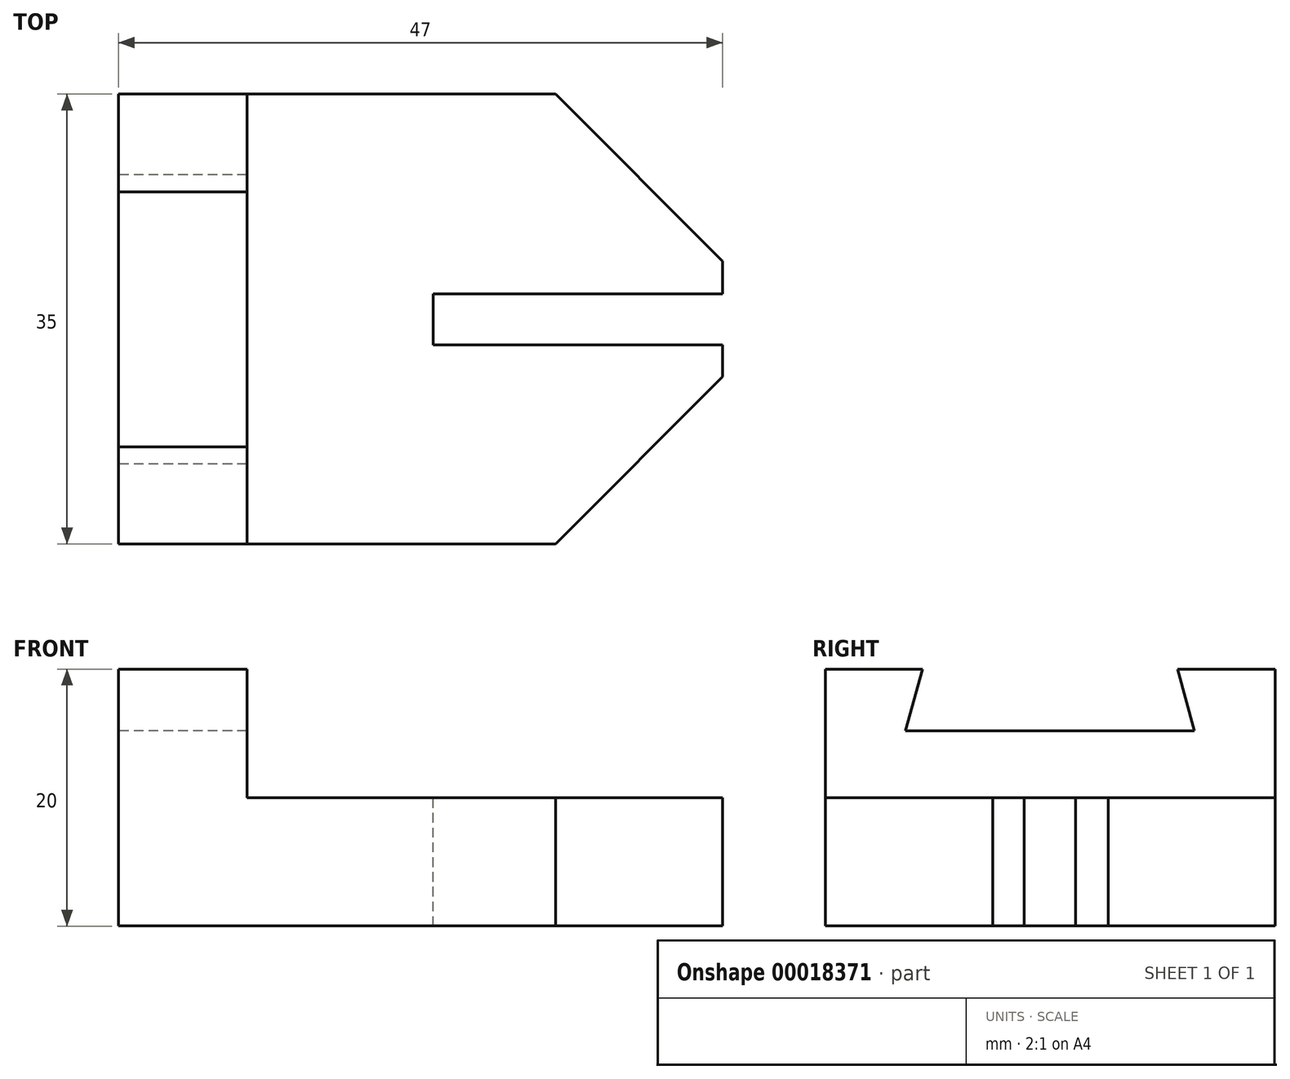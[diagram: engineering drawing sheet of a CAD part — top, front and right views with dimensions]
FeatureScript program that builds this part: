
annotation { "Feature Type Name" : "Feature", "Feature Type Description" : "" }
export const myFeature = defineFeature(function(context is Context, id is Id, definition is map)
    precondition{}
    {
        {
            var Q0;
            Q0=qCreatedBy(makeId("Right.planeOp"),FACE);
            var sketch = newSketch(context, id + "F0", { "sketchPlane" : qUnion([Q0])});
            skLineSegment(sketch, "E0.bottom", {"start": v(-51.53, 19.41) * mm, "end": v(35.8, 19.41) * mm});
            skLineSegment(sketch, "E0.top", {"start": v(-51.53, 0) * mm, "end": v(35.8, 0) * mm});
            skLineSegment(sketch, "E0.left", {"start": v(-51.53, 19.41) * mm, "end": v(-51.53, 0) * mm});
            skLineSegment(sketch, "E0.right", {"start": v(35.8, 19.41) * mm, "end": v(35.8, 0) * mm});
            skSolve(sketch);
        }
        {
            var Q0;
            Q0=makeQuery(id+"F0.imprint","IMPRINT",FACE,{"disambiguationData":[TD([[makeQuery(id+"F0.imprint","IMPRINT",EDGE,{"derivedFrom":sQuery(id+"F0.wireOp",EDGE,"E0.bottom")}),-1.0]])]});
            extrude(context, id + "F1", {"entities" : qUnion([Q0]), "depth" : 80 * mm});
        }
        {
            var Q0;
            Q0=makeQuery(id+"F1.opExtrude","SWEPT_FACE",FACE,{"disambiguationData":[OSD([sQuery(id+"F0.wireOp",EDGE,"E0.bottom")])]});
            var sketch = newSketch(context, id + "F2", { "sketchPlane" : qUnion([Q0])});
            skLineSegment(sketch, "E1", {"start": v(80, 35.8) * mm, "end": v(45.4, 35.8) * mm});
            skLineSegment(sketch, "E2", {"start": v(45.4, 35.8) * mm, "end": v(80, 10.23) * mm});
            skLineSegment(sketch, "E3", {"start": v(80, 10.23) * mm, "end": v(80, 35.8) * mm});
            skLineSegment(sketch, "E4", {"start": v(80, 3.87) * mm, "end": v(35.07, 3.87) * mm});
            skLineSegment(sketch, "E5", {"start": v(35.07, 3.87) * mm, "end": v(35.07, -8.04) * mm});
            skLineSegment(sketch, "E6", {"start": v(35.07, -8.04) * mm, "end": v(80, -8.04) * mm});
            skLineSegment(sketch, "E7", {"start": v(80, -8.04) * mm, "end": v(80, 3.87) * mm});
            skLineSegment(sketch, "E8", {"start": v(80, -17.18) * mm, "end": v(48.58, -51.53) * mm});
            skLineSegment(sketch, "E9", {"start": v(48.58, -51.53) * mm, "end": v(80, -51.53) * mm});
            skLineSegment(sketch, "E10", {"start": v(80, -51.53) * mm, "end": v(80, -17.18) * mm});
            skSolve(sketch);
        }
        {
            var Q0;
            Q0=makeQuery(id+"F2.imprint","IMPRINT",FACE,{"disambiguationData":[TD([[makeQuery(id+"F2.imprint","IMPRINT",EDGE,{"derivedFrom":sQuery(id+"F2.wireOp",EDGE,"E8")}),1.0]])]});
            var Q1;
            Q1=makeQuery(id+"F2.imprint","IMPRINT",FACE,{"disambiguationData":[TD([[makeQuery(id+"F2.imprint","IMPRINT",EDGE,{"derivedFrom":sQuery(id+"F2.wireOp",EDGE,"E4")}),1.0]])]});
            var Q2;
            Q2=makeQuery(id+"F2.imprint","IMPRINT",FACE,{"disambiguationData":[TD([[makeQuery(id+"F2.imprint","IMPRINT",EDGE,{"derivedFrom":sQuery(id+"F2.wireOp",EDGE,"E1")}),1.0]])]});
            extrude(context, id + "F3", {"entities" : qUnion([Q0, Q1, Q2]), "operationType" : NewBodyOperationType.REMOVE, "endBound" : BoundingType.THROUGH_ALL, "oppositeDirection" : true, "depth" : 25 * mm});
        }
        {
            var Q0;
            Q0=makeQuery(id+"F1.opExtrude","SWEPT_FACE",FACE,{"disambiguationData":[OSD([sQuery(id+"F0.wireOp",EDGE,"E0.bottom")])]});
            var sketch = newSketch(context, id + "F4", { "sketchPlane" : qUnion([Q0])});
            skLineSegment(sketch, "E11", {"start": v(15.34, -51.53) * mm, "end": v(15.34, 35.8) * mm});
            skLineSegment(sketch, "E12", {"start": v(15.34, 35.8) * mm, "end": v(0, 35.8) * mm});
            skLineSegment(sketch, "E13", {"start": v(0, 35.8) * mm, "end": v(0, -51.53) * mm});
            skLineSegment(sketch, "E14", {"start": v(0, -51.53) * mm, "end": v(15.34, -51.53) * mm});
            skSolve(sketch);
        }
        {
            var Q0;
            Q0=makeQuery(id+"F4.imprint","IMPRINT",FACE,{"disambiguationData":[TD([[makeQuery(id+"F4.imprint","IMPRINT",EDGE,{"derivedFrom":sQuery(id+"F4.wireOp",EDGE,"E11")}),1.0]])]});
            extrude(context, id + "F5", {"entities" : qUnion([Q0]), "operationType" : NewBodyOperationType.ADD, "depth" : 25 * mm});
        }
        {
            var Q0;
            Q0=makeQuery(id+"F5.boolean.opBoolean","MERGE",FACE,{"derivedFrom":[makeQuery(id+"F1.opExtrude","CAP_FACE",FACE,{"disambiguationData":[OSD([sQuery(id+"F0.wireOp",EDGE,"E0.bottom"),sQuery(id+"F0.wireOp",EDGE,"E0.top"),sQuery(id+"F0.wireOp",EDGE,"E0.left"),sQuery(id+"F0.wireOp",EDGE,"E0.right")])],"isStart":true}),makeQuery(id+"F5.opExtrude","SWEPT_FACE",FACE,{"disambiguationData":[OSD([sQuery(id+"F4.wireOp",EDGE,"E13")])]})]});
            var sketch = newSketch(context, id + "F6", { "sketchPlane" : qUnion([Q0])});
            skLineSegment(sketch, "E15", {"start": v(-12.51, 44.41) * mm, "end": v(-21.05, 29.1) * mm});
            skLineSegment(sketch, "E16", {"start": v(-21.05, 29.1) * mm, "end": v(37.34, 29.1) * mm});
            skLineSegment(sketch, "E17", {"start": v(37.34, 29.1) * mm, "end": v(28.6, 44.41) * mm});
            skLineSegment(sketch, "E18", {"start": v(28.6, 44.41) * mm, "end": v(-12.51, 44.41) * mm});
            skSolve(sketch);
        }
        {
            var Q0;
            Q0=makeQuery(id+"F6.imprint","IMPRINT",FACE,{"disambiguationData":[TD([[makeQuery(id+"F6.imprint","IMPRINT",EDGE,{"derivedFrom":sQuery(id+"F6.wireOp",EDGE,"E15")}),1.0]])]});
            extrude(context, id + "F7", {"entities" : qUnion([Q0]), "operationType" : NewBodyOperationType.REMOVE, "endBound" : BoundingType.THROUGH_ALL, "oppositeDirection" : true, "depth" : 25 * mm});
        }
        {
            var Q0;
            Q0=makeQuery(id+"F1.opExtrude","SWEPT_BODY",BODY,{"disambiguationData":[OSD([sQuery(id+"F0.wireOp",EDGE,"E0.bottom"),sQuery(id+"F0.wireOp",EDGE,"E0.top"),sQuery(id+"F0.wireOp",EDGE,"E0.left"),sQuery(id+"F0.wireOp",EDGE,"E0.right")])]});
            deleteBodies(context, id + "F8", {"entities" : qUnion([Q0])});
        }
        {
            var Q0;
            Q0=qCreatedBy(makeId("Right.planeOp"),FACE);
            var sketch = newSketch(context, id + "F9", { "sketchPlane" : qUnion([Q0])});
            skLineSegment(sketch, "E19.bottom", {"start": v(-18.8, 37.24) * mm, "end": v(16.2, 37.24) * mm});
            skLineSegment(sketch, "E19.top", {"start": v(-18.8, 27.24) * mm, "end": v(16.2, 27.24) * mm});
            skLineSegment(sketch, "E19.left", {"start": v(-18.8, 37.24) * mm, "end": v(-18.8, 27.24) * mm});
            skLineSegment(sketch, "E19.right", {"start": v(16.2, 37.24) * mm, "end": v(16.2, 27.24) * mm});
            skSolve(sketch);
        }
        {
            var Q0;
            Q0=makeQuery(id+"F9.imprint","IMPRINT",FACE,{"disambiguationData":[TD([[makeQuery(id+"F9.imprint","IMPRINT",EDGE,{"derivedFrom":sQuery(id+"F9.wireOp",EDGE,"E19.bottom")}),-1.0]])]});
            extrude(context, id + "F10", {"entities" : qUnion([Q0]), "depth" : 47 * mm});
        }
        {
            var Q0;
            Q0=makeQuery(id+"F10.opExtrude","SWEPT_FACE",FACE,{"disambiguationData":[OSD([sQuery(id+"F9.wireOp",EDGE,"E19.bottom")])]});
            var sketch = newSketch(context, id + "F11", { "sketchPlane" : qUnion([Q0])});
            skLineSegment(sketch, "E20", {"start": v(34, 16.2) * mm, "end": v(47, 3.2) * mm});
            skLineSegment(sketch, "E21", {"start": v(47, 3.2) * mm, "end": v(47, 16.2) * mm});
            skLineSegment(sketch, "E22", {"start": v(34, 16.2) * mm, "end": v(47, 16.2) * mm});
            skLineSegment(sketch, "E23", {"start": v(47, -18.8) * mm, "end": v(34, -18.8) * mm});
            skLineSegment(sketch, "E24", {"start": v(34, -18.8) * mm, "end": v(47, -5.8) * mm});
            skLineSegment(sketch, "E25", {"start": v(47, -18.8) * mm, "end": v(47, -5.8) * mm});
            skLineSegment(sketch, "E26", {"start": v(47, -3.32) * mm, "end": v(24.5, -3.32) * mm});
            skLineSegment(sketch, "E27", {"start": v(24.5, -3.32) * mm, "end": v(24.5, 0) * mm});
            skLineSegment(sketch, "E28", {"start": v(24.5, 0.68) * mm, "end": v(24.5, 0) * mm});
            skLineSegment(sketch, "E29", {"start": v(24.5, 0.68) * mm, "end": v(47, 0.68) * mm});
            skLineSegment(sketch, "E30", {"start": v(47, 0.68) * mm, "end": v(47, -3.32) * mm});
            skLineSegment(sketch, "E31", {"start": v(47, -5.8) * mm, "end": v(47, -3.32) * mm});
            skLineSegment(sketch, "E32", {"start": v(47, 0.68) * mm, "end": v(47, 3.2) * mm});
            skSolve(sketch);
        }
        {
            var Q0;
            Q0=makeQuery(id+"F11.imprint","IMPRINT",FACE,{"disambiguationData":[TD([[makeQuery(id+"F11.imprint","IMPRINT",EDGE,{"derivedFrom":sQuery(id+"F11.wireOp",EDGE,"E23")}),-1.0]])]});
            var Q1;
            Q1=makeQuery(id+"F11.imprint","IMPRINT",FACE,{"disambiguationData":[TD([[makeQuery(id+"F11.imprint","IMPRINT",EDGE,{"derivedFrom":sQuery(id+"F11.wireOp",EDGE,"E26")}),-1.0]])]});
            var Q2;
            Q2=makeQuery(id+"F11.imprint","IMPRINT",FACE,{"disambiguationData":[TD([[makeQuery(id+"F11.imprint","IMPRINT",EDGE,{"derivedFrom":sQuery(id+"F11.wireOp",EDGE,"E20")}),1.0]])]});
            extrude(context, id + "F12", {"entities" : qUnion([Q0, Q1, Q2]), "operationType" : NewBodyOperationType.REMOVE, "endBound" : BoundingType.THROUGH_ALL, "oppositeDirection" : true, "depth" : 25 * mm});
        }
        {
            var Q0;
            Q0=makeQuery(id+"F10.opExtrude","SWEPT_FACE",FACE,{"disambiguationData":[OSD([sQuery(id+"F9.wireOp",EDGE,"E19.bottom")])]});
            var sketch = newSketch(context, id + "F13", { "sketchPlane" : qUnion([Q0])});
            skLineSegment(sketch, "E33.bottom", {"start": v(0, 16.2) * mm, "end": v(10, 16.2) * mm});
            skLineSegment(sketch, "E33.top", {"start": v(0, -18.8) * mm, "end": v(10, -18.8) * mm});
            skLineSegment(sketch, "E33.left", {"start": v(0, 16.2) * mm, "end": v(0, -18.8) * mm});
            skLineSegment(sketch, "E33.right", {"start": v(10, 16.2) * mm, "end": v(10, -18.8) * mm});
            skSolve(sketch);
        }
        {
            var Q0;
            Q0=makeQuery(id+"F13.imprint","IMPRINT",FACE,{"disambiguationData":[TD([[makeQuery(id+"F13.imprint","IMPRINT",EDGE,{"derivedFrom":sQuery(id+"F13.wireOp",EDGE,"E33.bottom")}),1.0]])]});
            extrude(context, id + "F14", {"entities" : qUnion([Q0]), "operationType" : NewBodyOperationType.ADD, "depth" : 10 * mm});
        }
        {
            var Q0;
            Q0=makeQuery(id+"F14.boolean.opBoolean","MERGE",FACE,{"derivedFrom":[makeQuery(id+"F10.opExtrude","CAP_FACE",FACE,{"disambiguationData":[OSD([sQuery(id+"F9.wireOp",EDGE,"E19.bottom"),sQuery(id+"F9.wireOp",EDGE,"E19.top"),sQuery(id+"F9.wireOp",EDGE,"E19.left"),sQuery(id+"F9.wireOp",EDGE,"E19.right")])],"isStart":true}),makeQuery(id+"F14.opExtrude","SWEPT_FACE",FACE,{"disambiguationData":[OSD([sQuery(id+"F13.wireOp",EDGE,"E33.left")])]})]});
            var sketch = newSketch(context, id + "F15", { "sketchPlane" : qUnion([Q0])});
            skLineSegment(sketch, "E34", {"start": v(-8.6, 47.24) * mm, "end": v(-9.92, 42.42) * mm});
            skLineSegment(sketch, "E35", {"start": v(-9.92, 42.42) * mm, "end": v(12.58, 42.42) * mm});
            skLineSegment(sketch, "E36", {"start": v(12.58, 42.42) * mm, "end": v(11.25, 47.24) * mm});
            skLineSegment(sketch, "E37", {"start": v(-8.6, 47.24) * mm, "end": v(11.25, 47.24) * mm});
            skSolve(sketch);
        }
        {
            var Q0;
            Q0=makeQuery(id+"F15.imprint","IMPRINT",FACE,{"disambiguationData":[TD([[makeQuery(id+"F15.imprint","IMPRINT",EDGE,{"derivedFrom":sQuery(id+"F15.wireOp",EDGE,"E34")}),1.0]])]});
            extrude(context, id + "F16", {"entities" : qUnion([Q0]), "operationType" : NewBodyOperationType.REMOVE, "endBound" : BoundingType.THROUGH_ALL, "oppositeDirection" : true, "depth" : 25 * mm});
        }
    });
